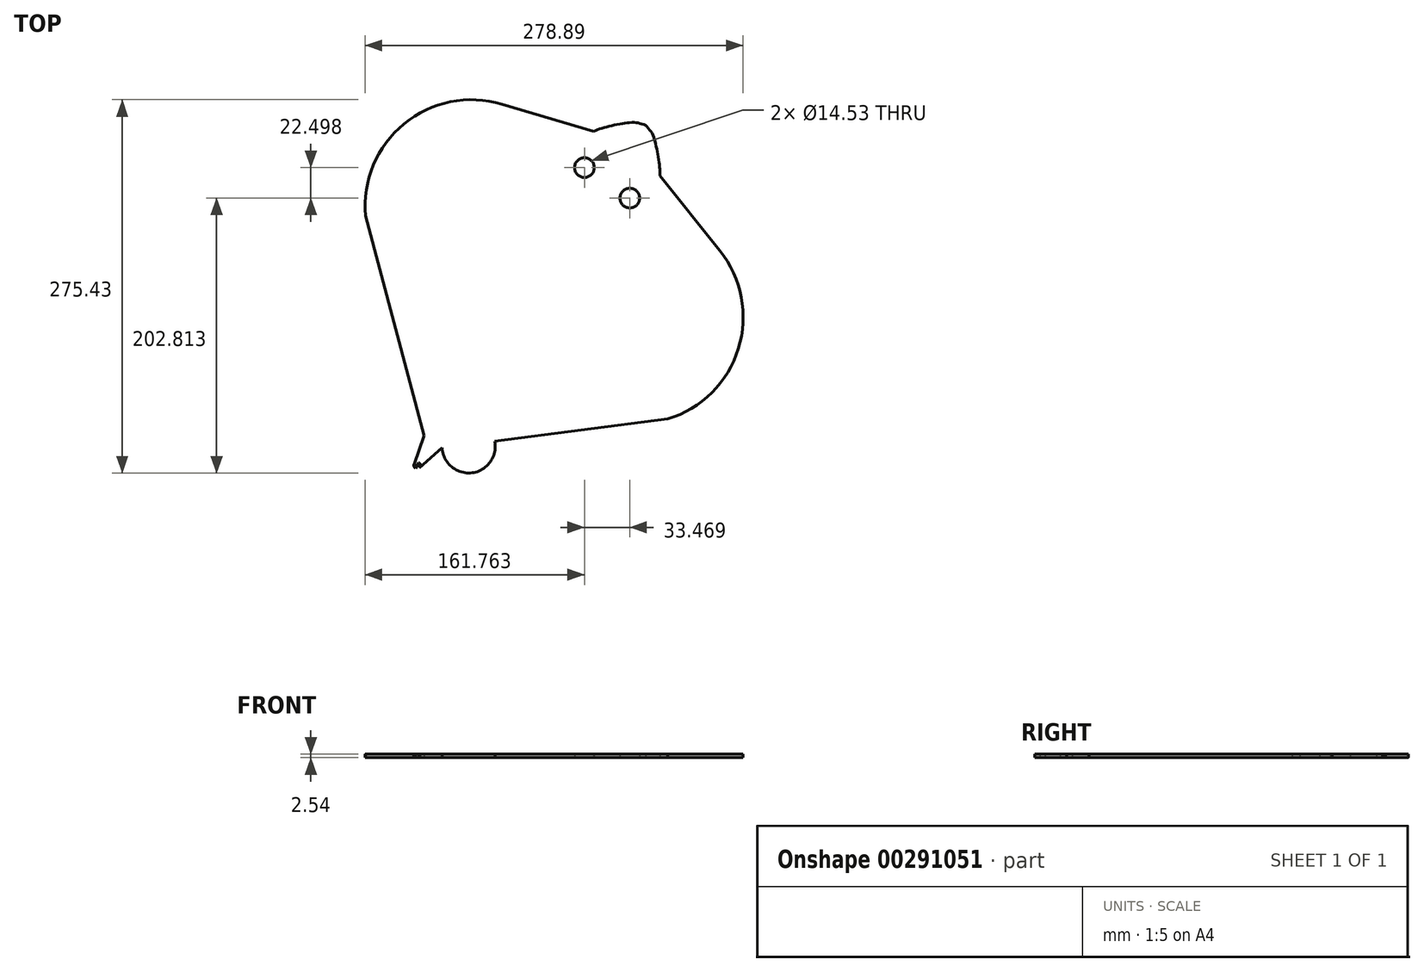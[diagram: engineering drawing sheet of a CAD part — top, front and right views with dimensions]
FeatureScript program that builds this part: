
annotation { "Feature Type Name" : "Feature", "Feature Type Description" : "" }
export const myFeature = defineFeature(function(context is Context, id is Id, definition is map)
    precondition{}
    {
        {
            var Q0;
            Q0=qCreatedBy(makeId("Top.planeOp"),FACE);
            var sketch = newSketch(context, id + "F0", { "sketchPlane" : qUnion([Q0])});
            skLineSegment(sketch, "E0", {"start": v(349.68, -156.6) * mm, "end": v(128.4, -184.93) * mm});
            skArc(sketch, "E1", {"start": v(349.68, -156.6) * mm, "mid": v(414.88, -91.76) * mm, "end": v(397.73, -1.4) * mm});
            skPoint(sketch, "E1.second.point", {"position": v(397.73, -1.4) * mm});
            skPoint(sketch, "E1.third.point", {"position": v(256.71, 11.2) * mm});
            skLineSegment(sketch, "E2", {"start": v(397.73, -1.4) * mm, "end": v(342.5, 67.53) * mm});
            skFitSpline(sketch, "E3", {"points": [v(329.45, 114.17) * mm, v(335.17, 106.79) * mm, v(338.93, 95.37) * mm, v(341.85, 79.5) * mm, v(342.5, 67.53) * mm], "startDerivative": vector(28.74, -31.44) * mm, "endDerivative": vector(0.9, -46.23) * mm});
            skFitSpline(sketch, "E4.MirrorCS", {"points": [v(329.45, 114.17) * mm, v(320.46, 116.67) * mm, v(308.47, 115.84) * mm, v(292.66, 112.56) * mm, v(281.34, 108.65) * mm], "startDerivative": vector(-39.97, 14.74) * mm, "endDerivative": vector(-43.15, -16.61) * mm});
            skLineSegment(sketch, "E5.MirrorCS", {"start": v(196.66, 133.76) * mm, "end": v(281.34, 108.65) * mm});
            skArc(sketch, "E6.MirrorCS", {"start": v(71.08, 30.67) * mm, "mid": v(106.52, 115.54) * mm, "end": v(196.66, 133.76) * mm});
            skLineSegment(sketch, "E7.MirrorCS", {"start": v(71.08, 30.67) * mm, "end": v(128.4, -184.93) * mm});
            skArc(sketch, "E8", {"start": v(141.66, -183.23) * mm, "mid": v(169.27, -206.27) * mm, "end": v(190.19, -177.02) * mm});
            skArc(sketch, "E9.MirrorCS", {"start": v(124.96, -172) * mm, "mid": v(93.2, -155.14) * mm, "end": v(112.4, -124.72) * mm});
            skCircle(sketch, "E10", {"center": v(314.7, 47.04) * mm, "radius": 9.08 * mm});
            skCircle(sketch, "E11.MirrorC", {"center": v(272.86, 75.16) * mm, "radius": 9.08 * mm});
            skLineSegment(sketch, "E12", {"start": v(141.28, -165.76) * mm, "end": v(105.85, -218.47) * mm});
            skPoint(sketch, "E13.centerSnap0", {"position": v(117.85, -186.78) * mm});
            skPoint(sketch, "E14.orphan", {"position": v(110.74, -201.56) * mm});
            skLineSegment(sketch, "E15", {"start": v(124.96, -172) * mm, "end": v(115.73, -198.47) * mm});
            skArc(sketch, "E16", {"start": v(120.32, -196.94) * mm, "mid": v(116.08, -197.77) * mm, "end": v(116.9, -202.02) * mm});
            skLineSegment(sketch, "E17.MirrorCS", {"start": v(141.66, -183.23) * mm, "end": v(120.64, -201.77) * mm});
            skArc(sketch, "E18.MirrorCS", {"start": v(120.32, -196.94) * mm, "mid": v(121.15, -201.18) * mm, "end": v(116.9, -202.02) * mm});
            skPoint(sketch, "E19", {"position": v(151.29, -150.87) * mm});
            skPoint(sketch, "E20", {"position": v(106.52, 115.54) * mm});
            skPoint(sketch, "E21", {"position": v(414.88, -91.76) * mm});
            skSolve(sketch);
        }
        {
            var Q0;
            {var subQ6=sQuery(id+"F0.wireOp",EDGE,"96ff0fba-3782-41fb-b143-67dd822ef4f5.trimOffspring");Q0=makeQuery(id+"F0.imprint","IMPRINT",FACE,{"disambiguationData":[TD([[makeQuery(id+"F0.imprint","IMPRINT",EDGE,{"derivedFrom":subQ6}),1.0]])]});}
            var Q1;
            {var subQ3=sQuery(id+"F0.wireOp",EDGE,"96ff0fba-3782-41fb-b143-67dd822ef4f5.trimOffspring");Q1=makeQuery(id+"F0.imprint","IMPRINT",FACE,{"disambiguationData":[TD([[makeQuery(id+"F0.imprint","IMPRINT",EDGE,{"derivedFrom":subQ3}),-1.0]])]});}
            var Q2;
            {var subQ3=sQuery(id+"F0.wireOp",EDGE,"20fb43c8-7627-4232-974f-628a24a2b0d7.trimOffspring");Q2=makeQuery(id+"F0.imprint","IMPRINT",FACE,{"disambiguationData":[TD([[makeQuery(id+"F0.imprint","IMPRINT",EDGE,{"derivedFrom":subQ3}),-1.0]])]});}
            var Q3;
            {var subQ3=sQuery(id+"F0.wireOp",EDGE,"20fb43c8-7627-4232-974f-628a24a2b0d7.trimOffspring");Q3=makeQuery(id+"F0.imprint","IMPRINT",FACE,{"disambiguationData":[TD([[makeQuery(id+"F0.imprint","IMPRINT",EDGE,{"derivedFrom":subQ3}),1.0]])]});}
            var Q4;
            {var subQ4=sQuery(id+"F0.wireOp",EDGE,"E2");Q4=makeQuery(id+"F0.imprint","IMPRINT",FACE,{"disambiguationData":[TD([[makeQuery(id+"F0.imprint","IMPRINT",EDGE,{"derivedFrom":subQ4}),1.0]])]});}
            var Q5;
            {var subQ4=sQuery(id+"F0.wireOp",EDGE,"E4.MirrorCS");Q5=makeQuery(id+"F0.imprint","IMPRINT",FACE,{"disambiguationData":[TD([[makeQuery(id+"F0.imprint","IMPRINT",EDGE,{"derivedFrom":subQ4}),1.0]])]});}
            var Q6;
            {var subQ0=sQuery(id+"F0.wireOp",EDGE,"E9.MirrorCS");Q6=makeQuery(id+"F0.imprint","IMPRINT",FACE,{"disambiguationData":[TD([[makeQuery(id+"F0.imprint","IMPRINT",EDGE,{"derivedFrom":subQ0}),-1.0]])]});}
            var Q7;
            {var subQ0=sQuery(id+"F0.wireOp",EDGE,"E8");Q7=makeQuery(id+"F0.imprint","IMPRINT",FACE,{"disambiguationData":[TD([[makeQuery(id+"F0.imprint","IMPRINT",EDGE,{"derivedFrom":subQ0}),1.0]])]});}
            var Q8;
            {var subQ3=sQuery(id+"F0.wireOp",EDGE,"E15");Q8=makeQuery(id+"F0.imprint","IMPRINT",FACE,{"disambiguationData":[TD([[makeQuery(id+"F0.imprint","IMPRINT",EDGE,{"derivedFrom":subQ3}),1.0]])]});}
            var Q9;
            {var subQ3=sQuery(id+"F0.wireOp",EDGE,"E17.MirrorCS");Q9=makeQuery(id+"F0.imprint","IMPRINT",FACE,{"disambiguationData":[TD([[makeQuery(id+"F0.imprint","IMPRINT",EDGE,{"derivedFrom":subQ3}),-1.0]])]});}
            var Q10;
            {var subQ0=sQuery(id+"F0.wireOp",EDGE,"E18.MirrorCS");var subQ5=makeQuery(id+"F0.imprint","INTERSECT",VERTEX,{"derivedFrom":[sQuery(id+"F0.wireOp",EDGE,"E17.MirrorCS"),subQ0]});Q10=makeQuery(id+"F0.imprint","IMPRINT",FACE,{"disambiguationData":[TD([[makeQuery(id+"F0.imprint","IMPRINT",EDGE,{"disambiguationData":[TD([[subQ5,1.0]])],"derivedFrom":subQ0}),-1.0]])]});}
            var Q11;
            {var subQ1=sQuery(id+"F0.wireOp",EDGE,"E16");var subQ5=makeQuery(id+"F0.imprint","INTERSECT",VERTEX,{"derivedFrom":[sQuery(id+"F0.wireOp",EDGE,"E15"),subQ1]});Q11=makeQuery(id+"F0.imprint","IMPRINT",FACE,{"disambiguationData":[TD([[makeQuery(id+"F0.imprint","IMPRINT",EDGE,{"disambiguationData":[TD([[subQ5,1.0]])],"derivedFrom":subQ1}),1.0]])]});}
            var Q12;
            {var subQ0=sQuery(id+"F0.wireOp",EDGE,"DjyJlNz0-C8nG-GKP9-kqsk-xTR7cpHYfLBt");var subQ1=sQuery(id+"F0.wireOp",EDGE,"E7.MirrorCS");var subQ2=makeQuery(id+"F0.imprint","INTERSECT",VERTEX,{"derivedFrom":[subQ1,subQ0]});Q12=makeQuery(id+"F0.imprint","IMPRINT",FACE,{"disambiguationData":[TD([[makeQuery(id+"F0.imprint","IMPRINT",EDGE,{"disambiguationData":[TD([[subQ2,-1.0]])],"derivedFrom":subQ1}),1.0]])]});}
            var Q13;
            {var subQ0=sQuery(id+"F0.wireOp",EDGE,"E12");var subQ8=sQuery(id+"F0.wireOp",EDGE,"47FEyY1M-ZaSq-AjOU-eLgn-XjdCFbVZ5Alc");var subQ9=makeQuery(id+"F0.imprint","INTERSECT",VERTEX,{"derivedFrom":[subQ8,subQ0]});Q13=makeQuery(id+"F0.imprint","IMPRINT",FACE,{"disambiguationData":[TD([[makeQuery(id+"F0.imprint","IMPRINT",EDGE,{"disambiguationData":[TD([[subQ9,1.0]])],"derivedFrom":subQ8}),-1.0]])]});}
            var Q14;
            {var subQ0=sQuery(id+"F0.wireOp",EDGE,"E12");var subQ1=sQuery(id+"F0.wireOp",EDGE,"47FEyY1M-ZaSq-AjOU-eLgn-XjdCFbVZ5Alc");var subQ2=makeQuery(id+"F0.imprint","INTERSECT",VERTEX,{"derivedFrom":[subQ1,subQ0]});Q14=makeQuery(id+"F0.imprint","IMPRINT",FACE,{"disambiguationData":[TD([[makeQuery(id+"F0.imprint","IMPRINT",EDGE,{"disambiguationData":[TD([[subQ2,1.0]])],"derivedFrom":subQ1}),1.0]])]});}
            extrude(context, id + "F1", {"entities" : qUnion([Q0, Q1, Q2, Q3, Q4, Q5, Q6, Q7, Q8, Q9, Q10, Q11, Q12, Q13, Q14]), "depth" : 3.17 * mm});
        }
        {
            var Q0;
            Q0=makeQuery(id+"F1.opExtrude","SWEPT_BODY",BODY,{"disambiguationData":[OSD([sQuery(id+"F0.wireOp",EDGE,"E0"),sQuery(id+"F0.wireOp",EDGE,"E1"),sQuery(id+"F0.wireOp",EDGE,"E2"),sQuery(id+"F0.wireOp",EDGE,"E3"),sQuery(id+"F0.wireOp",EDGE,"E4.MirrorCS"),sQuery(id+"F0.wireOp",EDGE,"E5.MirrorCS"),sQuery(id+"F0.wireOp",EDGE,"E6.MirrorCS"),sQuery(id+"F0.wireOp",EDGE,"E7.MirrorCS"),sQuery(id+"F0.wireOp",EDGE,"E8"),sQuery(id+"F0.wireOp",EDGE,"E9.MirrorCS"),sQuery(id+"F0.wireOp",EDGE,"E10"),sQuery(id+"F0.wireOp",EDGE,"E11.MirrorC"),sQuery(id+"F0.wireOp",EDGE,"E15"),sQuery(id+"F0.wireOp",EDGE,"E16"),sQuery(id+"F0.wireOp",EDGE,"E17.MirrorCS"),sQuery(id+"F0.wireOp",EDGE,"E18.MirrorCS")])]});
            var Q1;
            Q1=sQuery(id+"F0.wireOp",VERTEX,"E1.third.point");
            transform(context, id + "F2", {"entities" : qUnion([Q0]), "transformType" : TransformType.SCALE_UNIFORMLY, "scale" : .8, "scalePoint" : qUnion([Q1]), "makeCopy" : false});
        }
    });
